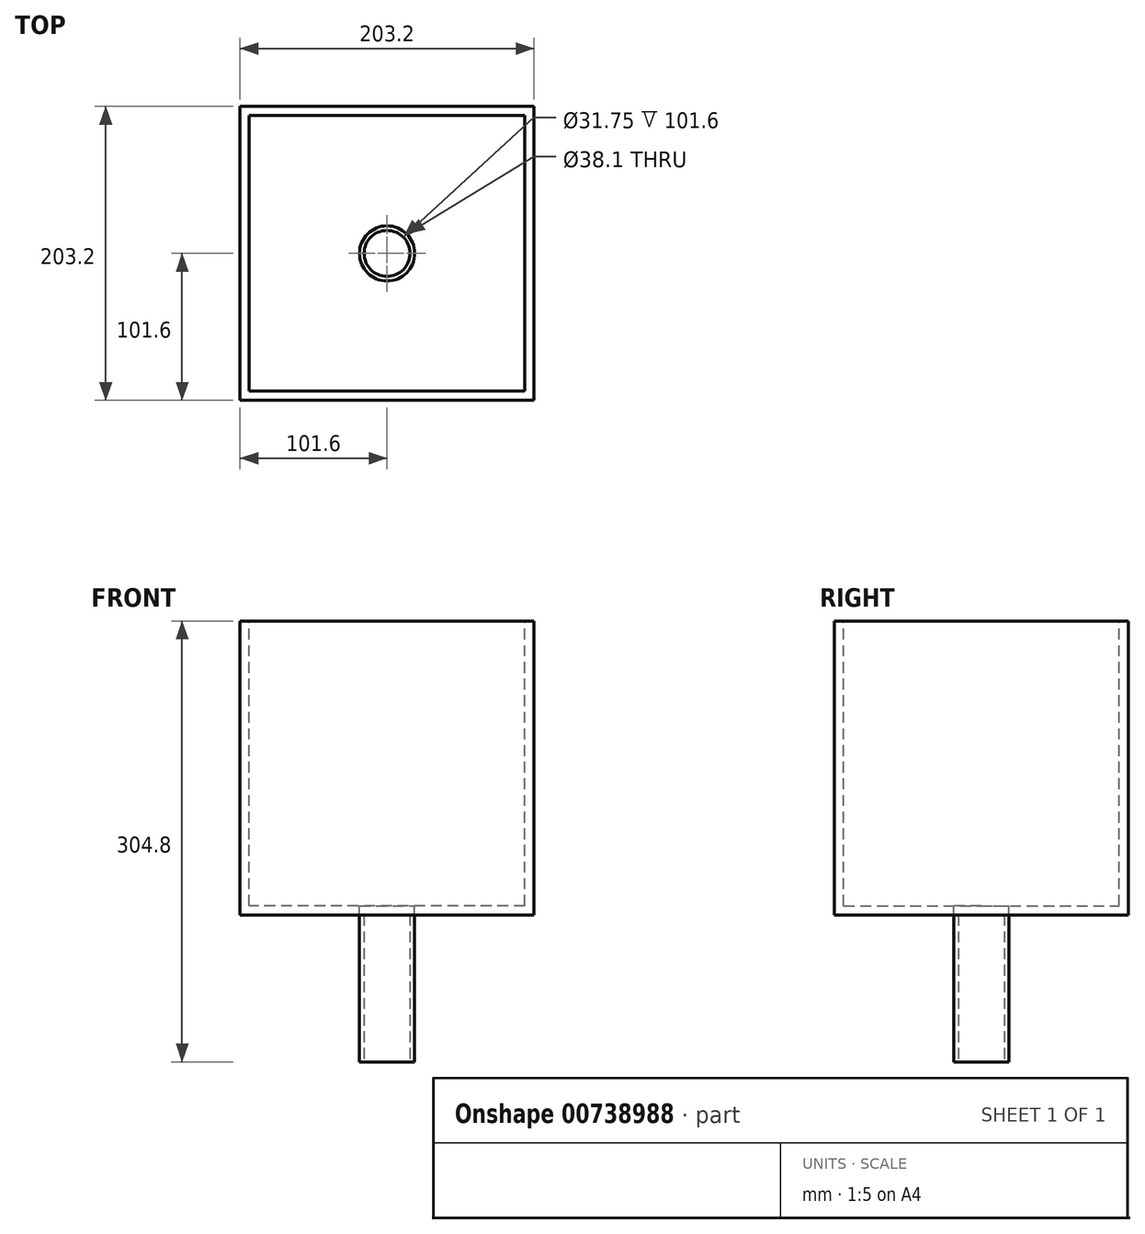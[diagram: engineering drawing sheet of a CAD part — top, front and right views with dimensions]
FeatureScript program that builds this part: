
annotation { "Feature Type Name" : "Feature", "Feature Type Description" : "" }
export const myFeature = defineFeature(function(context is Context, id is Id, definition is map)
    precondition{}
    {
        {
            var Q0;
            Q0=qCreatedBy(makeId("Front.planeOp"),FACE);
            var sketch = newSketch(context, id + "F0", { "sketchPlane" : qUnion([Q0])});
            skLineSegment(sketch, "E0.bottom", {"start": v(0, 0) * mm, "end": v(-203.2, 0) * mm});
            skLineSegment(sketch, "E0.top", {"start": v(0, 203.2) * mm, "end": v(-203.2, 203.2) * mm});
            skLineSegment(sketch, "E0.left", {"start": v(0, 0) * mm, "end": v(0, 203.2) * mm});
            skLineSegment(sketch, "E0.right", {"start": v(-203.2, 0) * mm, "end": v(-203.2, 203.2) * mm});
            skSolve(sketch);
        }
        {
            var Q0;
            Q0 = qSketchRegion(id + "F0", true);
            extrude(context, id + "F1", {"entities" : qUnion([Q0]), "depth" : 203.2 * mm, "offsetDistance" : 25.4 * mm});
        }
        {
            var Q0;
            Q0=makeQuery(id+"F1.opExtrude","SWEPT_FACE",FACE,{"disambiguationData":[OSD([sQuery(id+"F0.wireOp",EDGE,"E0.top")])]});
            shell(context, id + "F2", {"entities" : qUnion([Q0]), "thickness" : 6.35 * mm});
        }
        {
            var Q0;
            Q0=makeQuery(id+"F1.opExtrude","SWEPT_FACE",FACE,{"disambiguationData":[OSD([sQuery(id+"F0.wireOp",EDGE,"E0.bottom")])]});
            var sketch = newSketch(context, id + "F3", { "sketchPlane" : qUnion([Q0])});
            skCircle(sketch, "E1", {"center": v(-101.6, 101.6) * mm, "radius": 19.05 * mm});
            skSolve(sketch);
        }
        {
            var Q0;
            Q0=sQuery(id+"F3.wireOp",VERTEX,"E1.center");
            var Q1;
            Q1=makeQuery(id+"F1.opExtrude","SWEPT_BODY",BODY,{"disambiguationData":[OSD([sQuery(id+"F0.wireOp",EDGE,"E0.bottom"),sQuery(id+"F0.wireOp",EDGE,"E0.top"),sQuery(id+"F0.wireOp",EDGE,"E0.left"),sQuery(id+"F0.wireOp",EDGE,"E0.right")])]});
            hole(context, id + "F4", {"style" : HoleStyle.SIMPLE, "endStyle" : HoleEndStyle.THROUGH, "holeDiameter" : 38.1 * mm, "majorDiameter" : 6.35 * mm, "isTappedThrough" : true, "tappedDepth" : 12.7 * mm, "tapClearance" : 3, "locations" : qUnion([Q0]), "scope" : qUnion([Q1])});
        }
        {
            var Q0;
            Q0=makeQuery(id+"F3.imprint","IMPRINT",FACE,{"disambiguationData":[TD([[makeQuery(id+"F3.imprint","IMPRINT",EDGE,{"derivedFrom":sQuery(id+"F3.wireOp",EDGE,"E1")}),1.0]])]});
            var Q1;
            Q1=sQuery(id+"F3.wireOp",EDGE,"E1");
            extrude(context, id + "F5", {"entities" : qUnion([Q0]), "surfaceEntities" : qUnion([Q1]), "depth" : 101.6 * mm, "offsetDistance" : 25.4 * mm});
        }
        {
            var Q0;
            Q0=sQuery(id+"F3.wireOp",VERTEX,"E1.center");
            var Q1;
            Q1=makeQuery(id+"F5.opExtrude","SWEPT_BODY",BODY,{"disambiguationData":[OSD([sQuery(id+"F3.wireOp",EDGE,"E1")])]});
            hole(context, id + "F6", {"style" : HoleStyle.SIMPLE, "endStyle" : HoleEndStyle.THROUGH, "oppositeDirection" : true, "holeDiameter" : 31.75 * mm, "majorDiameter" : 6.35 * mm, "isTappedThrough" : true, "tappedDepth" : 12.7 * mm, "tapClearance" : 3, "locations" : qUnion([Q0]), "scope" : qUnion([Q1])});
        }
    });
